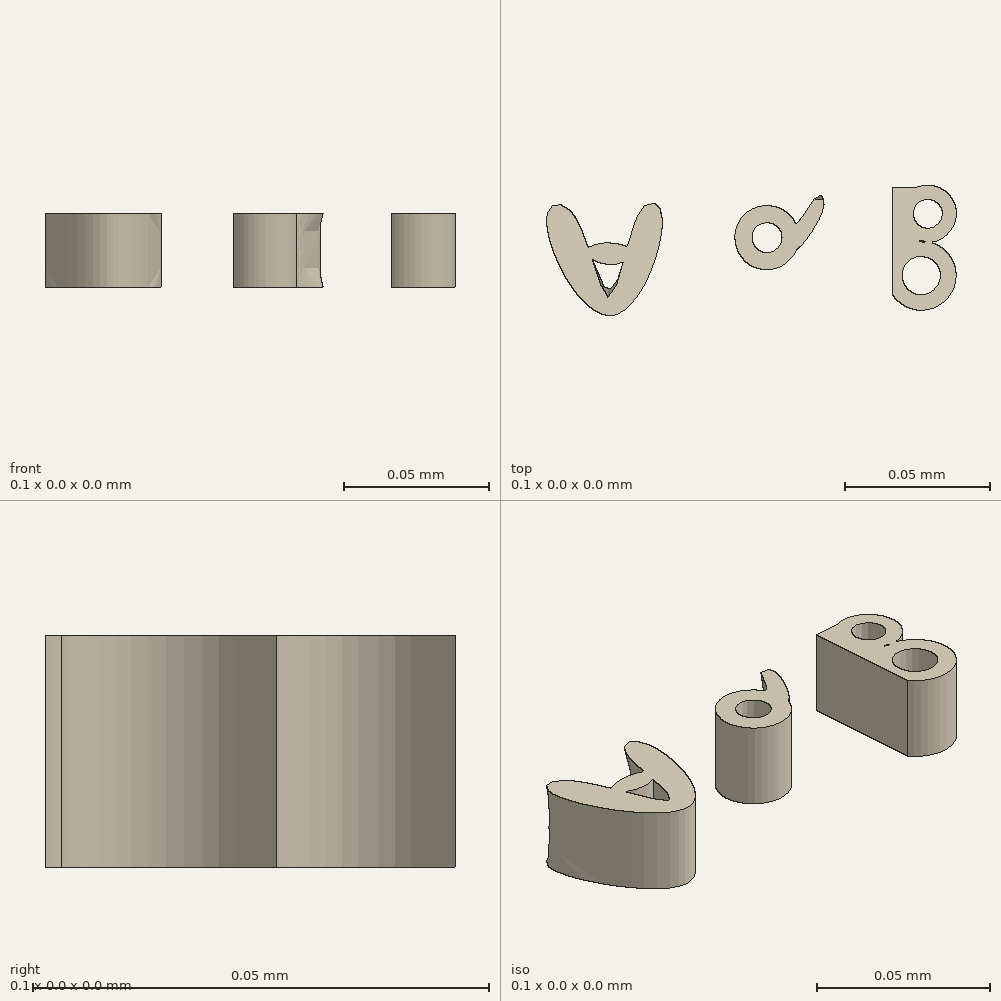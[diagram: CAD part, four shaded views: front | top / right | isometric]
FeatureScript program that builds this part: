
annotation { "Feature Type Name" : "Feature", "Feature Type Description" : "" }
export const myFeature = defineFeature(function(context is Context, id is Id, definition is map)
    precondition{}
    {
        {
            var Q0;
            Q0=qCreatedBy(makeId("Top.planeOp"),FACE);
            var sketch = newSketch(context, id + "F0", { "sketchPlane" : qUnion([Q0])});
            skFitSpline(sketch, "E0", {"points": [v(-76.2, -76.16) * mm, v(-76.17, -76.2) * mm, v(-76.16, -76.16) * mm, v(-76.16, -76.16) * mm, v(-76.17, -76.19) * mm, v(-76.19, -76.16) * mm, v(-76.2, -76.16) * mm]});
            skFitSpline(sketch, "E1", {"points": [v(-76.17, -76.17) * mm, v(-76.18, -76.17) * mm, v(-76.18, -76.17) * mm, v(-76.17, -76.17) * mm, v(-76.17, -76.17) * mm]});
            skCircle(sketch, "E2", {"center": v(-76.12, -76.17) * mm, "radius": 0.01 * mm});
            skFitSpline(sketch, "E3", {"points": [v(-76.1, -76.17) * mm, v(-76.1, -76.16) * mm, v(-76.1, -76.15) * mm, v(-76.11, -76.16) * mm], "startDerivative": vector(-0.03, -0.09) * mm, "endDerivative": vector(-0.05, -0.03) * mm});
            skCircle(sketch, "E4", {"center": v(-76.12, -76.17) * mm, "radius": 0 * mm});
            skLineSegment(sketch, "E5.bottom", {"start": v(-76.08, -76.15) * mm, "end": v(-76.07, -76.15) * mm});
            skLineSegment(sketch, "E5.top", {"start": v(-76.08, -76.2) * mm, "end": v(-76.07, -76.2) * mm});
            skLineSegment(sketch, "E5.left", {"start": v(-76.08, -76.15) * mm, "end": v(-76.08, -76.2) * mm});
            skLineSegment(sketch, "E5.right", {"start": v(-76.07, -76.15) * mm, "end": v(-76.07, -76.2) * mm});
            skCircle(sketch, "E6", {"center": v(-76.07, -76.18) * mm, "radius": 0.01 * mm});
            skCircle(sketch, "E7", {"center": v(-76.06, -76.16) * mm, "radius": 0 * mm});
            skCircle(sketch, "E8", {"center": v(-76.07, -76.18) * mm, "radius": 0 * mm});
            skLineSegment(sketch, "E9.bottom", {"start": v(-76.03, -76.14) * mm, "end": v(-76.02, -76.14) * mm});
            skLineSegment(sketch, "E9.top", {"start": v(-76.03, -76.19) * mm, "end": v(-76.02, -76.19) * mm});
            skLineSegment(sketch, "E9.left", {"start": v(-76.03, -76.14) * mm, "end": v(-76.03, -76.19) * mm});
            skLineSegment(sketch, "E9.right", {"start": v(-76.02, -76.14) * mm, "end": v(-76.02, -76.19) * mm});
            skCircle(sketch, "E10", {"center": v(-76.02, -76.16) * mm, "radius": 0.01 * mm});
            skCircle(sketch, "E11", {"center": v(-76.02, -76.16) * mm, "radius": 0 * mm});
            skFitSpline(sketch, "E12", {"points": [v(-75.97, -76.19) * mm, v(-75.99, -76.19) * mm, v(-76, -76.18) * mm, v(-76, -76.17) * mm, v(-76, -76.15) * mm, v(-75.98, -76.14) * mm, v(-75.97, -76.14) * mm], "startDerivative": vector(-0.09, -0.01) * mm, "endDerivative": vector(0.08, -0.01) * mm});
            skFitSpline(sketch, "E13.0", {"points": [v(-75.97, -76.18) * mm, v(-75.98, -76.18) * mm, v(-75.99, -76.18) * mm, v(-76, -76.17) * mm, v(-76, -76.16) * mm, v(-76, -76.15) * mm, v(-75.99, -76.15) * mm, v(-75.98, -76.15) * mm, v(-75.97, -76.15) * mm]});
            skLineSegment(sketch, "E14", {"start": v(-75.97, -76.19) * mm, "end": v(-75.97, -76.18) * mm});
            skLineSegment(sketch, "E15", {"start": v(-75.97, -76.15) * mm, "end": v(-75.97, -76.14) * mm});
            skFitSpline(sketch, "E16", {"points": [v(-75.94, -76.16) * mm, v(-75.95, -76.16) * mm, v(-75.95, -76.15) * mm, v(-75.94, -76.14) * mm, v(-75.94, -76.15) * mm, v(-75.95, -76.15) * mm, v(-75.95, -76.15) * mm, v(-75.95, -76.16) * mm, v(-75.94, -76.16) * mm, v(-75.94, -76.16) * mm, v(-75.94, -76.16) * mm]});
            skSolve(sketch);
        }
        {
            var Q0;
            {var subQ0=sQuery(id+"F0.wireOp",EDGE,"E1");var subQ1=sQuery(id+"F0.wireOp",EDGE,"E0");var subQ2=makeQuery(id+"F0.imprint","INTERSECT",VERTEX,{"disambiguationData":[OD(0.0)],"derivedFrom":[subQ1,subQ0]});Q0=makeQuery(id+"F0.imprint","IMPRINT",FACE,{"disambiguationData":[TD([[makeQuery(id+"F0.imprint","IMPRINT",EDGE,{"disambiguationData":[TD([[subQ2,-1.0]])],"derivedFrom":subQ1}),1.0]])]});}
            var Q1;
            {var subQ0=sQuery(id+"F0.wireOp",EDGE,"E1");var subQ1=sQuery(id+"F0.wireOp",EDGE,"E0");var subQ2=makeQuery(id+"F0.imprint","INTERSECT",VERTEX,{"disambiguationData":[OD(1.0)],"derivedFrom":[subQ1,subQ0]});Q1=makeQuery(id+"F0.imprint","IMPRINT",FACE,{"disambiguationData":[TD([[makeQuery(id+"F0.imprint","IMPRINT",EDGE,{"disambiguationData":[TD([[subQ2,1.0]])],"derivedFrom":subQ1}),1.0]])]});}
            var Q2;
            {var subQ0=sQuery(id+"F0.wireOp",EDGE,"E3");var subQ1=sQuery(id+"F0.wireOp",EDGE,"E2");var subQ2=makeQuery(id+"F0.imprint","INTERSECT",VERTEX,{"disambiguationData":[OD(0.0)],"derivedFrom":[subQ1,subQ0]});Q2=makeQuery(id+"F0.imprint","IMPRINT",FACE,{"disambiguationData":[TD([[makeQuery(id+"F0.imprint","IMPRINT",EDGE,{"disambiguationData":[TD([[subQ2,-1.0]])],"derivedFrom":subQ1}),-1.0]])]});}
            var Q3;
            {var subQ0=sQuery(id+"F0.wireOp",EDGE,"E3");var subQ1=sQuery(id+"F0.wireOp",EDGE,"E2");var subQ2=makeQuery(id+"F0.imprint","INTERSECT",VERTEX,{"disambiguationData":[OD(0.0)],"derivedFrom":[subQ1,subQ0]});Q3=makeQuery(id+"F0.imprint","IMPRINT",FACE,{"disambiguationData":[TD([[makeQuery(id+"F0.imprint","IMPRINT",EDGE,{"disambiguationData":[TD([[subQ2,1.0]])],"derivedFrom":subQ1}),1.0]])]});}
            var Q4;
            {var subQ0=sQuery(id+"F0.wireOp",EDGE,"E5.left");var subQ1=sQuery(id+"F0.wireOp",EDGE,"E5.bottom");var subQ2=makeQuery(id+"F0.imprint","INTERSECT",VERTEX,{"derivedFrom":[subQ1,subQ0]});Q4=makeQuery(id+"F0.imprint","IMPRINT",FACE,{"disambiguationData":[TD([[makeQuery(id+"F0.imprint","IMPRINT",EDGE,{"disambiguationData":[TD([[subQ2,-1.0]])],"derivedFrom":subQ1}),-1.0]])]});}
            var Q5;
            {var subQ0=sQuery(id+"F0.wireOp",EDGE,"E5.right");var subQ1=sQuery(id+"F0.wireOp",EDGE,"E5.bottom");var subQ2=makeQuery(id+"F0.imprint","INTERSECT",VERTEX,{"derivedFrom":[subQ1,subQ0]});Q5=makeQuery(id+"F0.imprint","IMPRINT",FACE,{"disambiguationData":[TD([[makeQuery(id+"F0.imprint","IMPRINT",EDGE,{"disambiguationData":[TD([[subQ2,1.0]])],"derivedFrom":subQ1}),1.0]])]});}
            var Q6;
            {var subQ0=sQuery(id+"F0.wireOp",EDGE,"E1");var subQ1=sQuery(id+"F0.wireOp",EDGE,"E0");var subQ2=makeQuery(id+"F0.imprint","INTERSECT",VERTEX,{"disambiguationData":[OD(0.0)],"derivedFrom":[subQ1,subQ0]});Q6=makeQuery(id+"F0.imprint","IMPRINT",FACE,{"disambiguationData":[TD([[makeQuery(id+"F0.imprint","IMPRINT",EDGE,{"disambiguationData":[TD([[subQ2,-1.0]])],"derivedFrom":subQ1}),-1.0]])]});}
            var Q7;
            {var subQ0=sQuery(id+"F0.wireOp",EDGE,"E1");var subQ1=sQuery(id+"F0.wireOp",EDGE,"E0");var subQ2=makeQuery(id+"F0.imprint","INTERSECT",VERTEX,{"disambiguationData":[OD(2.0)],"derivedFrom":[subQ1,subQ0]});Q7=makeQuery(id+"F0.imprint","IMPRINT",FACE,{"disambiguationData":[TD([[makeQuery(id+"F0.imprint","IMPRINT",EDGE,{"disambiguationData":[TD([[subQ2,-1.0]])],"derivedFrom":subQ1}),1.0]])]});}
            var Q8;
            Q8=makeQuery(id+"F0.imprint","IMPRINT",FACE,{"disambiguationData":[TD([[makeQuery(id+"F0.imprint","IMPRINT",EDGE,{"derivedFrom":sQuery(id+"F0.wireOp",EDGE,"E4")}),-1.0]])]});
            var Q9;
            {var subQ0=sQuery(id+"F0.wireOp",EDGE,"E5.right");var subQ1=sQuery(id+"F0.wireOp",EDGE,"E5.bottom");var subQ2=makeQuery(id+"F0.imprint","INTERSECT",VERTEX,{"derivedFrom":[subQ1,subQ0]});Q9=makeQuery(id+"F0.imprint","IMPRINT",FACE,{"disambiguationData":[TD([[makeQuery(id+"F0.imprint","IMPRINT",EDGE,{"disambiguationData":[TD([[subQ2,1.0]])],"derivedFrom":subQ1}),-1.0]])]});}
            var Q10;
            {var subQ0=sQuery(id+"F0.wireOp",EDGE,"E7");var subQ1=sQuery(id+"F0.wireOp",EDGE,"E5.right");var subQ2=makeQuery(id+"F0.imprint","INTERSECT",VERTEX,{"derivedFrom":[subQ1,subQ0]});Q10=makeQuery(id+"F0.imprint","IMPRINT",FACE,{"disambiguationData":[TD([[makeQuery(id+"F0.imprint","IMPRINT",EDGE,{"disambiguationData":[TD([[subQ2,1.0]])],"derivedFrom":subQ1}),1.0]])]});}
            var Q11;
            {var subQ0=sQuery(id+"F0.wireOp",EDGE,"E6");var subQ2=makeQuery(id+"F0.imprint","IMPRINT",VERTEX,{"derivedFrom":subQ0});Q11=makeQuery(id+"F0.imprint","IMPRINT",FACE,{"disambiguationData":[TD([[makeQuery(id+"F0.imprint","IMPRINT",EDGE,{"disambiguationData":[TD([[subQ2,1.0]])],"derivedFrom":subQ0}),1.0]])]});}
            var Q12;
            {var subQ1=sQuery(id+"F0.wireOp",EDGE,"E5.right");var subQ3=sQuery(id+"F0.wireOp",EDGE,"E7");var subQ5=makeQuery(id+"F0.imprint","INTERSECT",VERTEX,{"derivedFrom":[subQ1,subQ3]});Q12=makeQuery(id+"F0.imprint","IMPRINT",FACE,{"disambiguationData":[TD([[makeQuery(id+"F0.imprint","IMPRINT",EDGE,{"disambiguationData":[TD([[subQ5,-1.0]])],"derivedFrom":subQ1}),1.0]])]});}
            var Q13;
            {var subQ0=sQuery(id+"F0.wireOp",EDGE,"E6");var subQ5=sQuery(id+"F0.wireOp",EDGE,"E5.left");var subQ6=makeQuery(id+"F0.imprint","INTERSECT",VERTEX,{"disambiguationData":[OD(0.0)],"derivedFrom":[subQ5,subQ0]});Q13=makeQuery(id+"F0.imprint","IMPRINT",FACE,{"disambiguationData":[TD([[makeQuery(id+"F0.imprint","IMPRINT",EDGE,{"disambiguationData":[TD([[subQ6,-1.0]])],"derivedFrom":subQ5}),1.0]])]});}
            extrude(context, id + "F1", {"entities" : qUnion([Q0, Q1, Q2, Q3, Q4, Q5, Q6, Q7, Q8, Q9, Q10, Q11, Q12, Q13]), "depth" : 0.03 * mm});
        }
    });
